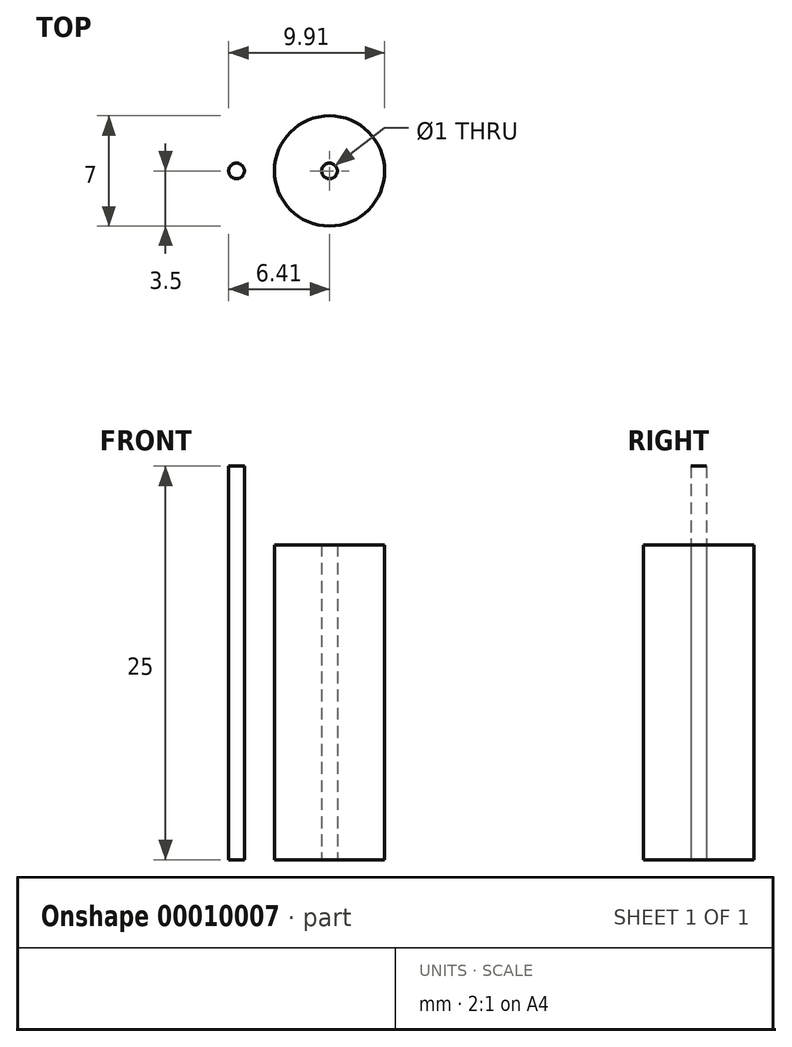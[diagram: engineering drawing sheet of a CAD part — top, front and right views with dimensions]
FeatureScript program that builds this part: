
annotation { "Feature Type Name" : "Feature", "Feature Type Description" : "" }
export const myFeature = defineFeature(function(context is Context, id is Id, definition is map)
    precondition{}
    {
        {
            var Q0;
            Q0=qCreatedBy(makeId("Top.planeOp"),FACE);
            var sketch = newSketch(context, id + "F0", { "sketchPlane" : qUnion([Q0])});
            skCircle(sketch, "E0", {"center": v(0, 0) * mm, "radius": 3.5 * mm});
            skCircle(sketch, "E1", {"center": v(0, 0) * mm, "radius": 0.5 * mm});
            skSolve(sketch);
        }
        {
            var Q0;
            Q0 = qSketchRegion(id + "F0", true);
            extrude(context, id + "F1", {"entities" : qUnion([Q0]), "depth" : 20 * mm});
        }
        {
            var Q0;
            Q0=qCreatedBy(makeId("Top.planeOp"),FACE);
            var sketch = newSketch(context, id + "F2", { "sketchPlane" : qUnion([Q0])});
            skCircle(sketch, "E2", {"center": v(-5.9, 0) * mm, "radius": 0.5 * mm});
            skSolve(sketch);
        }
        {
            var Q0;
            Q0 = qSketchRegion(id + "F2", true);
            extrude(context, id + "F3", {"entities" : qUnion([Q0]), "depth" : 25 * mm});
        }
    });
